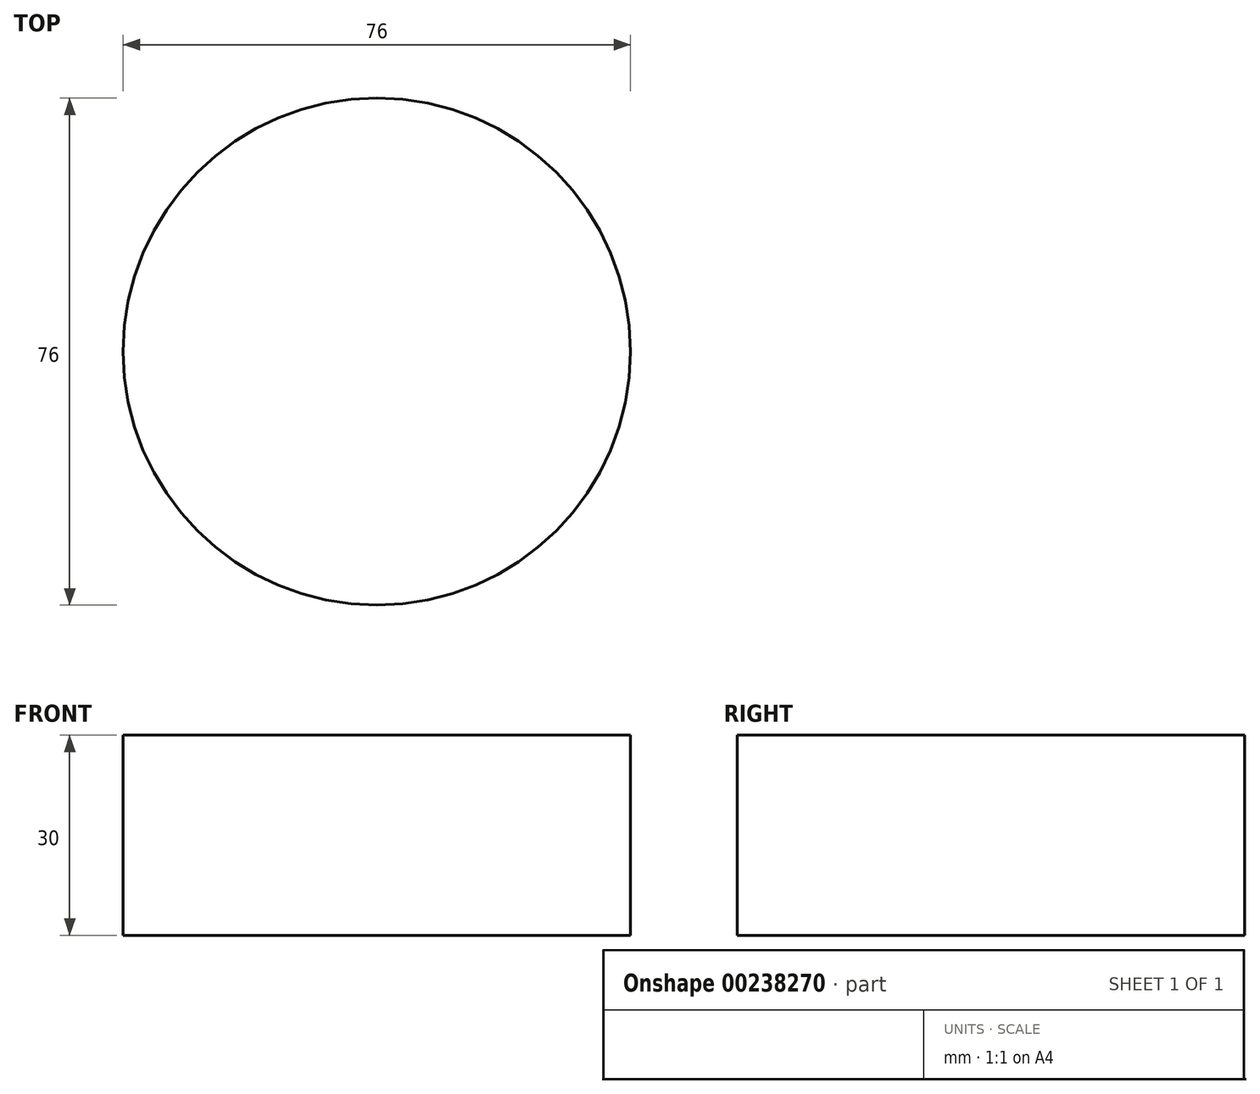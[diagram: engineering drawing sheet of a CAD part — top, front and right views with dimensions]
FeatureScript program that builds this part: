
annotation { "Feature Type Name" : "Feature", "Feature Type Description" : "" }
export const myFeature = defineFeature(function(context is Context, id is Id, definition is map)
    precondition{}
    {
        {
            var Q0;
            Q0=qCreatedBy(makeId("Top.planeOp"),FACE);
            var sketch = newSketch(context, id + "F0", { "sketchPlane" : qUnion([Q0])});
            skCircle(sketch, "E0", {"center": v(0, 0) * mm, "radius": 38 * mm});
            skSolve(sketch);
        }
        {
            var Q0;
            Q0=makeQuery(id+"F0.imprint","IMPRINT",FACE,{"disambiguationData":[TD([[makeQuery(id+"F0.imprint","IMPRINT",EDGE,{"derivedFrom":sQuery(id+"F0.wireOp",EDGE,"vloOt6jr-Imqc-Mewn-y0Mu-KJ2CrDvV60Ht")}),-1.0]])]});
            var Q1;
            Q1=makeQuery(id+"F0.imprint","IMPRINT",FACE,{"disambiguationData":[TD([[makeQuery(id+"F0.imprint","IMPRINT",EDGE,{"derivedFrom":sQuery(id+"F0.wireOp",EDGE,"E0")}),1.0]])]});
            extrude(context, id + "F1", {"entities" : qUnion([Q0, Q1]), "depth" : 30 * mm});
        }
    });
